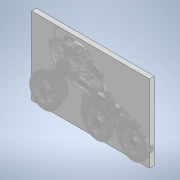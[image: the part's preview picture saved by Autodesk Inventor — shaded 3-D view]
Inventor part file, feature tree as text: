
AUTODESK INVENTOR PART (.ipt)
format: ipt  version: 2020.1 (Build 241239000, 239)  size: 2,723,840 bytes
history: native  units: mm
features: other x3, extrude x1, sketch x1
ambient origin geometry x8: Origin, YZ Plane, XZ Plane, XY Plane, X Axis, Y Axis, Z Axis, Center Point
bodies: Body1 (feature_tree)
feature tree (5):
  other  "Sólido1"
  other  "Rover 3 - Verde"
  extrude  "Extrusión1"  [1 undecoded]
  sketch  "Boceto1"  dims[d0=1.0mm d1=5.25mm d2=0.0mm d3=0.0mm]
  other  "MeshFeature1"
note: 1 required parameter value undecoded (feature->parameter linkage not recoverable at this tier; creation-order binding heuristic only, values carry confidence <= 0.55)
